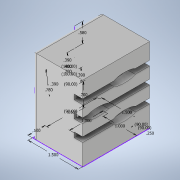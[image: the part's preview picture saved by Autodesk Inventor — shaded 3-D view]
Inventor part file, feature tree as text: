
AUTODESK INVENTOR PART (.ipt)
format: ipt  version: 2020 (Build 240168000, 168)  size: 223,744 bytes
history: native  units: in
note: dims shown in document units (in); Inventor stores cm internally (conversion verified against a paired STEP export)
features: extrude x4, hole x1, sketch x1, fillet x1
ambient origin geometry x8: Origin, YZ Plane, XZ Plane, XY Plane, X Axis, Y Axis, Z Axis, Center Point
bodies: Solid1 (feature_tree)
feature tree (7):
  extrude  "Extrusion1"  Depth=0.125in
  hole  "Hole1"  [1 undecoded]
  sketch  "Sketch2"  dims[d0=1.5in d1=1.5in d2=0.25in d3=90.0deg d4=1.0in d5=90.0deg d6=1.0in d7=2.24in d8=0.0in d9=0.3625in d10=0.75in d11=0.438in d12=0.25in d13=0.5635in d14=0.5in d15=0.0in d16=0.7in d17=90.0deg d18=0.39in d19=90.0deg d20=0.2in d21=180.0deg d22=0.39in d23=180.0deg d24=1.25in d25=0.0in d26=1.5in d27=0.0in d28=0.15in d29=0.15in d30=0.25in d31=0.0in d32=0.58in d34=1.5in d35=0.5in d36=0.4in d37=0.39in d38=0.78in d39=0.15in d40=0.125in]
  extrude  "Extrusion2"  TaperAngle=90.0deg  [1 undecoded]
  extrude  "Extrusion3"  Depth=0.125in
  extrude  "Extrusion4"  TaperAngle=90.0deg  [1 undecoded]
  fillet  "Fillet1"  Radius=1.0in
note: 3 required parameter values undecoded (feature->parameter linkage not recoverable at this tier; creation-order binding heuristic only, values carry confidence <= 0.55)
